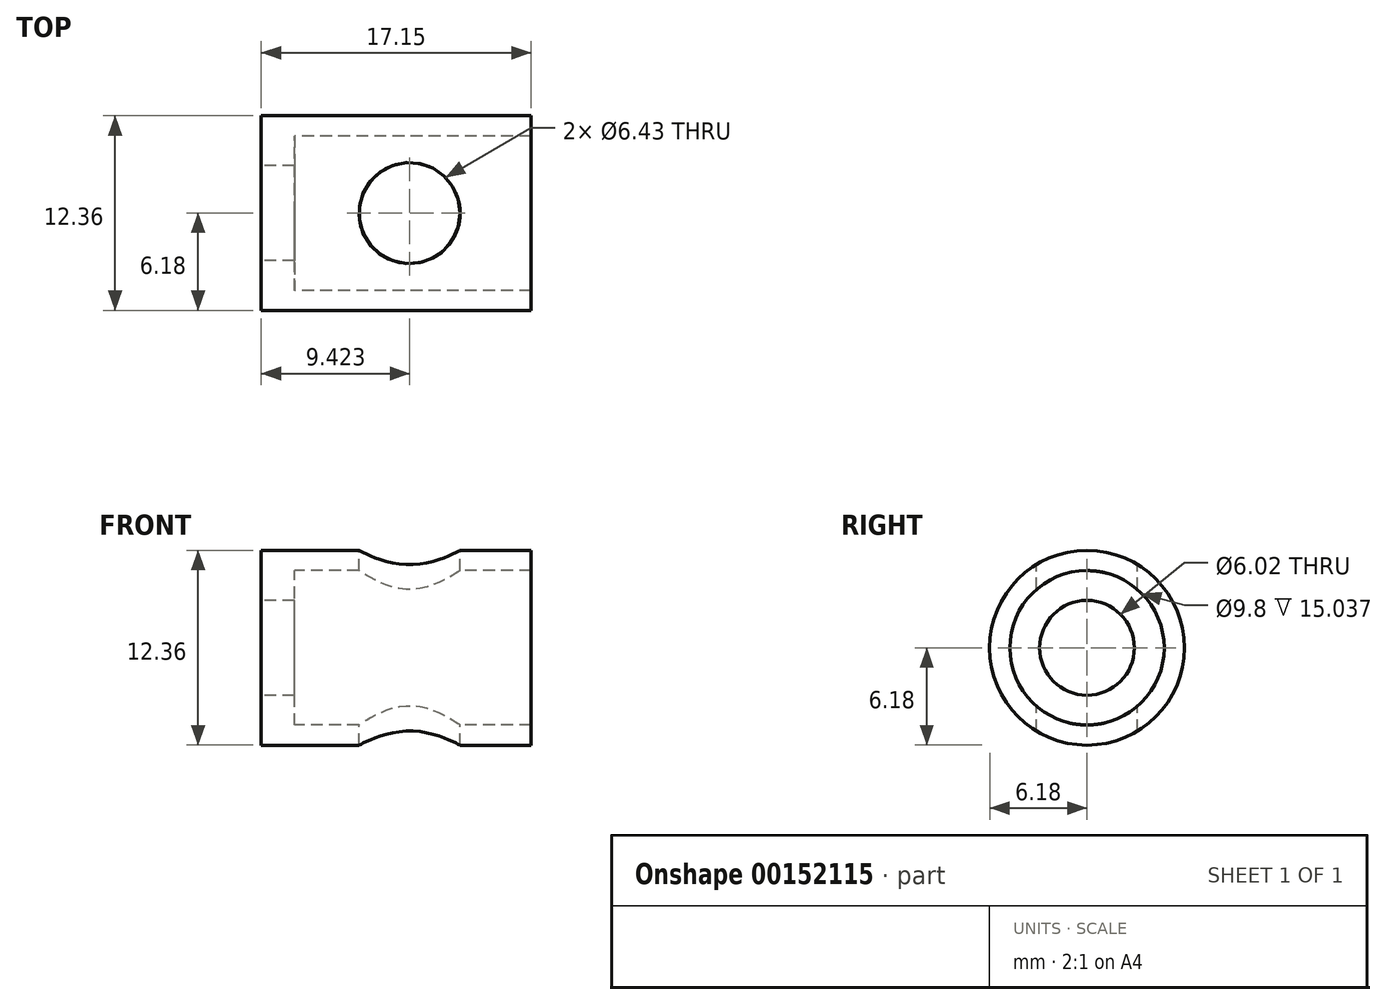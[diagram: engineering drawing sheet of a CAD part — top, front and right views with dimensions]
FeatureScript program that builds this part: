
annotation { "Feature Type Name" : "Feature", "Feature Type Description" : "" }
export const myFeature = defineFeature(function(context is Context, id is Id, definition is map)
    precondition{}
    {
        {
            var Q0;
            Q0=qCreatedBy(makeId("Right.planeOp"),FACE);
            var sketch = newSketch(context, id + "F0", { "sketchPlane" : qUnion([Q0])});
            skCircle(sketch, "E0", {"center": v(0, 0) * mm, "radius": 6.18 * mm});
            skCircle(sketch, "E1", {"center": v(0, 0) * mm, "radius": 4.9 * mm});
            skCircle(sketch, "E2", {"center": v(0, 0) * mm, "radius": 3 * mm});
            skSolve(sketch);
        }
        {
            var Q0;
            Q0=makeQuery(id+"F0.imprint","IMPRINT",FACE,{"disambiguationData":[TD([[makeQuery(id+"F0.imprint","IMPRINT",EDGE,{"derivedFrom":sQuery(id+"F0.wireOp",EDGE,"E0")}),1.0]])]});
            var Q1;
            Q1=makeQuery(id+"F0.imprint","IMPRINT",FACE,{"disambiguationData":[TD([[makeQuery(id+"F0.imprint","IMPRINT",EDGE,{"derivedFrom":sQuery(id+"F0.wireOp",EDGE,"E1")}),1.0]])]});
            extrude(context, id + "F1", {"entities" : qUnion([Q0, Q1]), "depth" : 2.1 * mm});
        }
        {
            var Q0;
            Q0=makeQuery(id+"F0.imprint","IMPRINT",FACE,{"disambiguationData":[TD([[makeQuery(id+"F0.imprint","IMPRINT",EDGE,{"derivedFrom":sQuery(id+"F0.wireOp",EDGE,"E0")}),1.0]])]});
            extrude(context, id + "F2", {"entities" : qUnion([Q0]), "operationType" : NewBodyOperationType.ADD, "depth" : 17.14 * mm});
        }
        {
            var Q0;
            Q0=qCreatedBy(makeId("Top.planeOp"),FACE);
            var sketch = newSketch(context, id + "F3", { "sketchPlane" : qUnion([Q0])});
            skCircle(sketch, "E3", {"center": v(9.42, 0) * mm, "radius": 3.21 * mm});
            skSolve(sketch);
        }
        {
            var Q0;
            Q0=makeQuery(id+"F3.imprint","IMPRINT",FACE,{"disambiguationData":[TD([[makeQuery(id+"F3.imprint","IMPRINT",EDGE,{"derivedFrom":sQuery(id+"F3.wireOp",EDGE,"E3")}),1.0]])]});
            extrude(context, id + "F4", {"entities" : qUnion([Q0]), "operationType" : NewBodyOperationType.REMOVE, "endBound" : BoundingType.SYMMETRIC, "oppositeDirection" : true, "depth" : 25.4 * mm});
        }
    });
